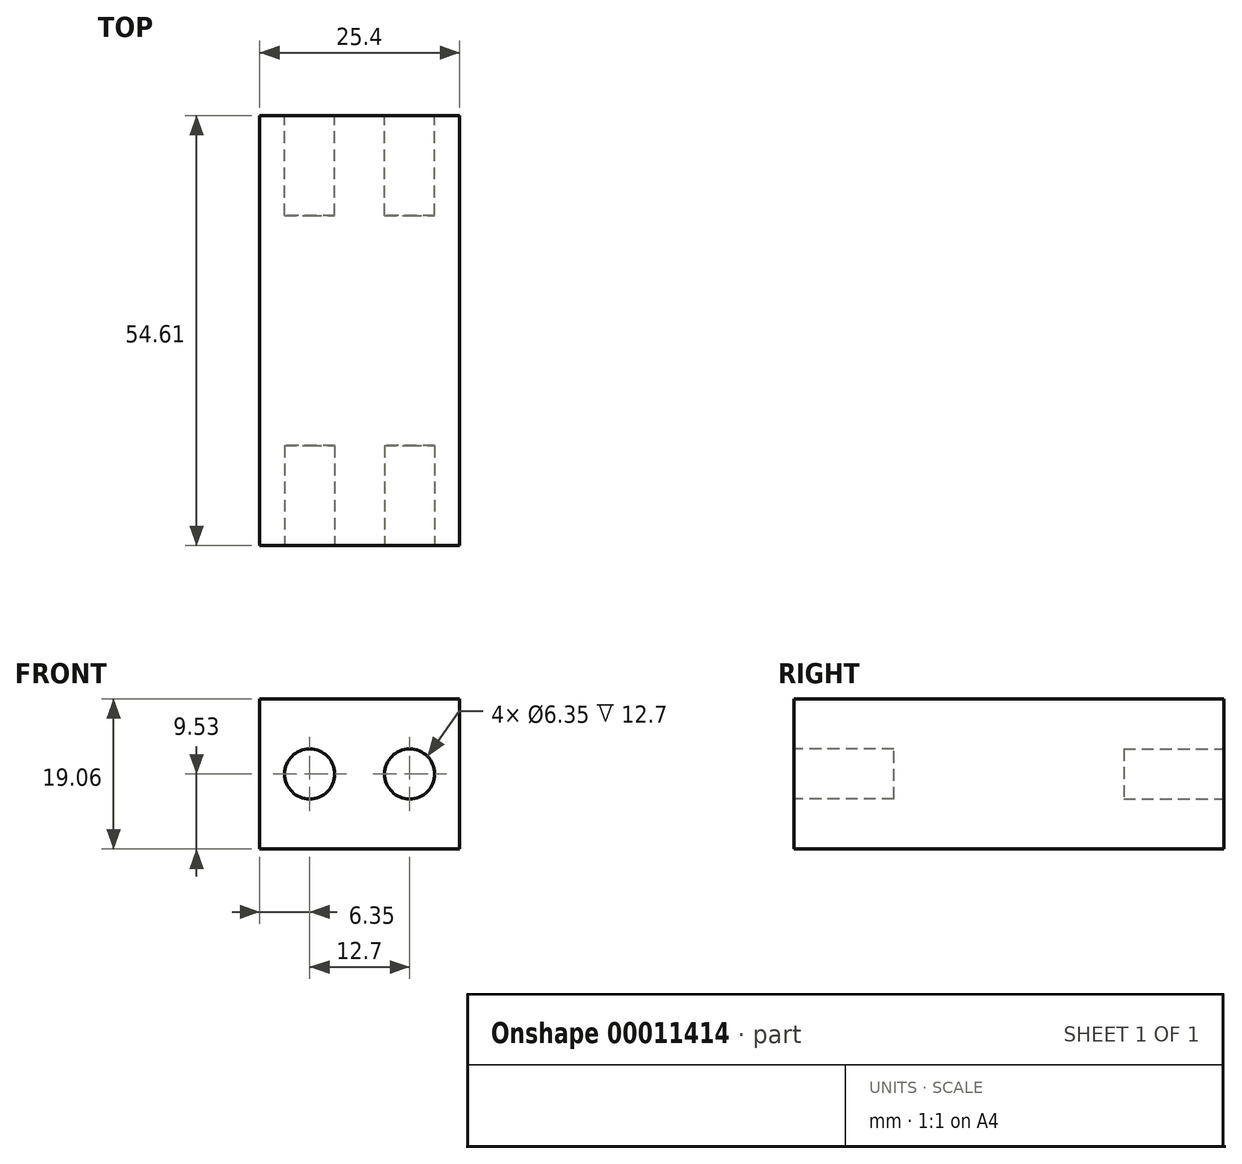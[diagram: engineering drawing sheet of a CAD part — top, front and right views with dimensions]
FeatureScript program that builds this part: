
annotation { "Feature Type Name" : "Feature", "Feature Type Description" : "" }
export const myFeature = defineFeature(function(context is Context, id is Id, definition is map)
    precondition{}
    {
        {
            var Q0;
            Q0=qCreatedBy(makeId("Front.planeOp"),FACE);
            var sketch = newSketch(context, id + "F0", { "sketchPlane" : qUnion([Q0])});
            skLineSegment(sketch, "E0.bottom", {"start": v(-12.7, 9.52) * mm, "end": v(12.7, 9.53) * mm});
            skLineSegment(sketch, "E0.top", {"start": v(-12.7, -9.53) * mm, "end": v(12.7, -9.52) * mm});
            skLineSegment(sketch, "E0.left", {"start": v(-12.7, 9.52) * mm, "end": v(-12.7, -9.53) * mm});
            skLineSegment(sketch, "E0.right", {"start": v(12.7, 9.53) * mm, "end": v(12.7, -9.52) * mm});
            skSolve(sketch);
        }
        {
            var Q0;
            Q0 = qSketchRegion(id + "F0", true);
            extrude(context, id + "F1", {"entities" : qUnion([Q0]), "depth" : 54.6 * mm});
        }
        {
            var Q0;
            Q0=makeQuery(id+"F1.opExtrude","CAP_FACE",FACE,{"disambiguationData":[OSD([sQuery(id+"F0.wireOp",EDGE,"E0.bottom"),sQuery(id+"F0.wireOp",EDGE,"E0.top"),sQuery(id+"F0.wireOp",EDGE,"E0.left"),sQuery(id+"F0.wireOp",EDGE,"E0.right")])],"isStart":false});
            var sketch = newSketch(context, id + "F2", { "sketchPlane" : qUnion([Q0])});
            skCircle(sketch, "E1", {"center": v(-6.35, 0) * mm, "radius": 3.18 * mm});
            skCircle(sketch, "E2", {"center": v(6.35, 0) * mm, "radius": 3.18 * mm});
            skSolve(sketch);
        }
        {
            var Q0;
            Q0 = qSketchRegion(id + "F2", true);
            extrude(context, id + "F3", {"entities" : qUnion([Q0]), "operationType" : NewBodyOperationType.REMOVE, "oppositeDirection" : true, "depth" : 12.7 * mm});
        }
        {
            var Q0;
            Q0=makeQuery(id+"F1.opExtrude","CAP_FACE",FACE,{"disambiguationData":[OSD([sQuery(id+"F0.wireOp",EDGE,"E0.bottom"),sQuery(id+"F0.wireOp",EDGE,"E0.top"),sQuery(id+"F0.wireOp",EDGE,"E0.left"),sQuery(id+"F0.wireOp",EDGE,"E0.right")])],"isStart":true});
            var sketch = newSketch(context, id + "F4", { "sketchPlane" : qUnion([Q0])});
            skCircle(sketch, "E3", {"center": v(-6.35, 0) * mm, "radius": 3.18 * mm});
            skCircle(sketch, "E4", {"center": v(6.35, 0) * mm, "radius": 3.18 * mm});
            skSolve(sketch);
        }
        {
            var Q0;
            Q0 = qSketchRegion(id + "F4", true);
            extrude(context, id + "F5", {"entities" : qUnion([Q0]), "operationType" : NewBodyOperationType.REMOVE, "oppositeDirection" : true, "depth" : 12.7 * mm});
        }
    });
